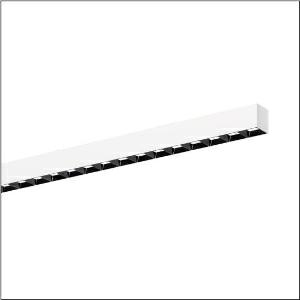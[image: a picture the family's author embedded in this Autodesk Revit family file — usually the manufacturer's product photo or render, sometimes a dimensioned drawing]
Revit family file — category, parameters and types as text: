
# Revit family: silica_r__21_51mx22dc4awb_3425
name_source: partatom
category: Lighting Fixtures
units: mm (PartAtom-declared; Revit-internal decimal feet)

## family parameters
Cut with Voids When Loaded = No
Host = Face
Light Source = No
Part Type = Normal
Room Calculation Point = No
Round Connector Dimension = Use Diameter
Shared = No

## types (1)
- --- (1 x LED, 10800 lm, 64.7 W, 4000K)
    Apparent Load = 65 VA
    CIE Flux Codes = 86 100 100 100 100
    Color Rendering = 80
    Color Temperature = 4000K
    Default Elevation = 1800 mm
    Description = Silica® 21, office luminaire, primary light control with darklight reflector, of PMMA, black, CAT 2 (L<= 3000cd/m²), light emission: direct distribution, primary light characteristic: symmetric, installation type: surface-mounted, LED, rated luminous flux: 10.800lm, luminous efficacy: 167lm/W, light colour: 840, colour temperature: 4000K, with terminal, 3+2-pole, max. 2.5mm², mains connection: 220..240V, AC, 50/60Hz, rated input power: 64.7W, luminaire housing, of aluminium, traffic white (RAL 9016), length: 3.004mm, width: 53mm, height: 53mm, protection rating (complete): IP20, insulation class (complete): insulation class I (protective earthing), certification: CE, permissible operating ambient temperature: 0..+35°C, standard: EN 50419, packaging unit: 1 piece
    Height = 0 mm  [stored 0 ft]
    Lamp = 1 x LED
    Lamp Light Flux = 10800 lm
    Lamp Power = 64.7 W
    Lamp count = 1
    Length = 3004 mm
    Luminous efficacy = 167 lm/W
    Manufacturer = Siteco
    ModVariant = No
    Model = 51MX22DC4AWB
    Mounting Place = Ceiling
    Mounting Type = Recessed
    Number of Poles = 1
    OnlyDefault = Yes
    Power Factor = 1
    Product Name = Silica® 21
    Product group = office luminaire | ceiling recessed
    ProductGroupID = 401
    Protection Class = Protection class I
    Protection Degree = IP 20
    RLX_Detail_Level = 1
    RLX_Emergency_Light_Flux = 0 lm
    RLX_Emergency_Type = 0
    RLX_Emergency_Type_DB = No
    RlxData = <blob elided: 62973 chars, md5=76ce4a8c>
    Socket = socket
    Standby Power = 0 W
    System Light Flux = 10800 lm
    System Power = 65 W
    Type Comments = factory setting: luminous flux: 100 % | dim-lin: 254 | 366 mA
    Type Image = l_1297779.jpg
    URL = http://relux.com
    VarID = @adj_056333
    Voltage = 0 V
    Weight = 0.00 kg
    Width = 53 mm

note: [stored X ft] marks values corroborated as IEEE doubles in the binary element streams (Revit-internal decimal feet)

## geometry (parser evidence)
native form markers: Blend x4, Sweep x11
no freeform markers — native parametric forms only
